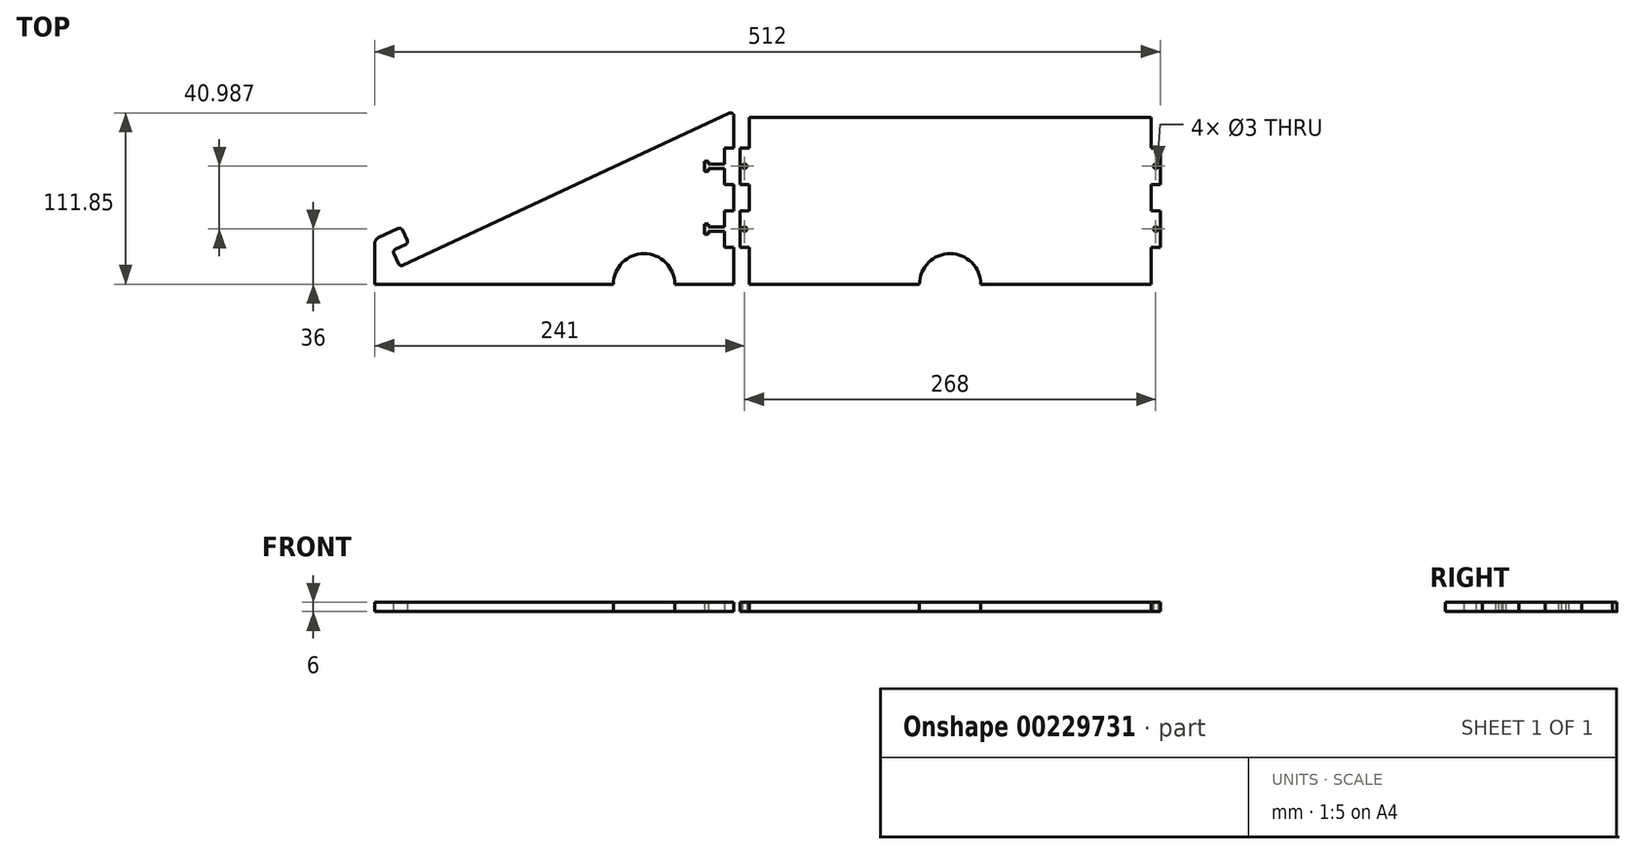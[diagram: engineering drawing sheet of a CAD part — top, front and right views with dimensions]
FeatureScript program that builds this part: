
annotation { "Feature Type Name" : "Feature", "Feature Type Description" : "" }
export const myFeature = defineFeature(function(context is Context, id is Id, definition is map)
    precondition{}
    {
        {
            assignVariable(context, id + "F0", {"name" : "MaterialThickness", "anyValue" : 6});
        }
        {
            var Q0;
            Q0=qCreatedBy(makeId("Top.planeOp"),FACE);
            var sketch = newSketch(context, id + "F1", { "sketchPlane" : qUnion([Q0])});
            skLineSegment(sketch, "E0", {"start": v(20.1, 25.94) * mm, "end": v(13.31, 22.77) * mm});
            skLineSegment(sketch, "E1", {"start": v(12.35, 20.1) * mm, "end": v(15.51, 13.31) * mm});
            skLineSegment(sketch, "E2", {"start": v(18.17, 12.35) * mm, "end": v(231.15, 111.66) * mm});
            skLineSegment(sketch, "E3", {"start": v(234, 0) * mm, "end": v(234, 109.85) * mm});
            skLineSegment(sketch, "E4", {"start": v(244, 108.99) * mm, "end": v(244, 88.99) * mm});
            skLineSegment(sketch, "E5", {"start": v(244, 0) * mm, "end": v(355, 0) * mm});
            skLineSegment(sketch, "E6", {"start": v(506, 0) * mm, "end": v(506, 24) * mm});
            skLineSegment(sketch, "E7", {"start": v(234, 24) * mm, "end": v(228, 24) * mm});
            skLineSegment(sketch, "E8", {"start": v(228, 24) * mm, "end": v(228, 34.5) * mm});
            skLineSegment(sketch, "E9", {"start": v(228, 48) * mm, "end": v(234, 48) * mm});
            skLineSegment(sketch, "E10", {"start": v(234, 56.5) * mm, "end": v(112.85, 56.5) * mm, "construction": true});
            skLineSegment(sketch, "E11.MirrorCS", {"start": v(228, 64.99) * mm, "end": v(234, 64.99) * mm});
            skLineSegment(sketch, "E12.MirrorCS", {"start": v(228, 88.99) * mm, "end": v(228, 78.49) * mm});
            skLineSegment(sketch, "E13.MirrorCS", {"start": v(234, 88.99) * mm, "end": v(228, 88.99) * mm});
            skLineSegment(sketch, "E14", {"start": v(244, 24) * mm, "end": v(238, 24) * mm});
            skLineSegment(sketch, "E15", {"start": v(238, 24) * mm, "end": v(238, 48) * mm});
            skLineSegment(sketch, "E16", {"start": v(238, 48) * mm, "end": v(244, 48) * mm});
            skLineSegment(sketch, "E17.MirrorCS", {"start": v(238, 64.99) * mm, "end": v(244, 64.99) * mm});
            skLineSegment(sketch, "E18.MirrorCS", {"start": v(238, 88.99) * mm, "end": v(238, 64.99) * mm});
            skLineSegment(sketch, "E19.MirrorCS", {"start": v(244, 88.99) * mm, "end": v(238, 88.99) * mm});
            skLineSegment(sketch, "E20", {"start": v(375, 108.99) * mm, "end": v(375, 0) * mm, "construction": true});
            skLineSegment(sketch, "E21.MirrorCS", {"start": v(506, 88.99) * mm, "end": v(512, 88.99) * mm});
            skLineSegment(sketch, "E22.MirrorCS", {"start": v(506, 24) * mm, "end": v(512, 24) * mm});
            skLineSegment(sketch, "E23.MirrorCS", {"start": v(512, 64.99) * mm, "end": v(506, 64.99) * mm});
            skLineSegment(sketch, "E24.MirrorCS", {"start": v(512, 24) * mm, "end": v(512, 48) * mm});
            skLineSegment(sketch, "E25.MirrorCS", {"start": v(512, 48) * mm, "end": v(506, 48) * mm});
            skLineSegment(sketch, "E26.MirrorCS", {"start": v(512, 88.99) * mm, "end": v(512, 64.99) * mm});
            skLineSegment(sketch, "E27", {"start": v(244, 108.99) * mm, "end": v(506, 108.99) * mm});
            skPoint(sketch, "E28.visualSharp", {"position": v(17.06, 37.2) * mm});
            skPoint(sketch, "E29.visualSharp", {"position": v(21.92, 26.78) * mm});
            skPoint(sketch, "E30.visualSharp", {"position": v(234, 112.99) * mm});
            skArc(sketch, "E30.filletArc", {"start": v(234, 109.85) * mm, "mid": v(233.07, 111.53) * mm, "end": v(231.15, 111.66) * mm});
            skCircle(sketch, "E31", {"center": v(241, 76.99) * mm, "radius": 1.5 * mm});
            skPoint(sketch, "E31.centerSnap0", {"position": v(238, 76.99) * mm});
            skPoint(sketch, "E31.centerSnap1", {"position": v(241, 88.99) * mm});
            skCircle(sketch, "E32.MirrorC", {"center": v(241, 36) * mm, "radius": 1.5 * mm});
            skLineSegment(sketch, "E33", {"start": v(228, 76.99) * mm, "end": v(234, 76.99) * mm, "construction": true});
            skLineSegment(sketch, "E34", {"start": v(228, 75.49) * mm, "end": v(217.5, 75.49) * mm});
            skLineSegment(sketch, "E35", {"start": v(217.5, 75.49) * mm, "end": v(217.5, 73.74) * mm});
            skLineSegment(sketch, "E36", {"start": v(217.5, 73.74) * mm, "end": v(215, 73.74) * mm});
            skLineSegment(sketch, "E37", {"start": v(215, 73.74) * mm, "end": v(215, 76.99) * mm});
            skLineSegment(sketch, "E38.MirrorCS", {"start": v(228, 78.49) * mm, "end": v(217.5, 78.49) * mm});
            skLineSegment(sketch, "E39.MirrorCS", {"start": v(217.5, 78.49) * mm, "end": v(217.5, 80.24) * mm});
            skLineSegment(sketch, "E40.MirrorCS", {"start": v(217.5, 80.24) * mm, "end": v(215, 80.24) * mm});
            skLineSegment(sketch, "E41.MirrorCS", {"start": v(215, 80.24) * mm, "end": v(215, 76.99) * mm});
            skLineSegment(sketch, "E42.MirrorCS", {"start": v(215, 39.25) * mm, "end": v(215, 36) * mm});
            skLineSegment(sketch, "E43.MirrorCS", {"start": v(228, 37.5) * mm, "end": v(217.5, 37.5) * mm});
            skLineSegment(sketch, "E44.MirrorCS", {"start": v(215, 32.75) * mm, "end": v(215, 36) * mm});
            skLineSegment(sketch, "E45.MirrorCS", {"start": v(217.5, 37.5) * mm, "end": v(217.5, 39.25) * mm});
            skLineSegment(sketch, "E46.MirrorCS", {"start": v(217.5, 34.5) * mm, "end": v(217.5, 32.75) * mm});
            skLineSegment(sketch, "E47.MirrorCS", {"start": v(217.5, 32.75) * mm, "end": v(215, 32.75) * mm});
            skLineSegment(sketch, "E48.MirrorCS", {"start": v(228, 34.5) * mm, "end": v(217.5, 34.5) * mm});
            skLineSegment(sketch, "E49.MirrorCS", {"start": v(217.5, 39.25) * mm, "end": v(215, 39.25) * mm});
            skCircle(sketch, "E50.MirrorC", {"center": v(509, 36) * mm, "radius": 1.5 * mm});
            skCircle(sketch, "E51.MirrorC", {"center": v(509, 76.99) * mm, "radius": 1.5 * mm});
            skPoint(sketch, "E52.orphan", {"position": v(244, 112.99) * mm});
            skPoint(sketch, "E53.orphan", {"position": v(506, 112.99) * mm});
            skPoint(sketch, "E54.orphan", {"position": v(375, 112.99) * mm});
            skPoint(sketch, "E55.visualSharp", {"position": v(16.36, 11.5) * mm});
            skArc(sketch, "E55.filletArc", {"start": v(15.51, 13.31) * mm, "mid": v(16.64, 12.28) * mm, "end": v(18.17, 12.35) * mm});
            skPoint(sketch, "E56.visualSharp", {"position": v(11.5, 21.92) * mm});
            skArc(sketch, "E56.filletArc", {"start": v(13.31, 22.77) * mm, "mid": v(12.28, 21.64) * mm, "end": v(12.35, 20.1) * mm});
            skArc(sketch, "E57", {"start": v(395, 0) * mm, "mid": v(375, 20) * mm, "end": v(355, 0) * mm});
            skLineSegment(sketch, "E58.trimOffspring", {"start": v(395, 0) * mm, "end": v(506, 0) * mm});
            skLineSegment(sketch, "E59.trimOffspring", {"start": v(228, 75.49) * mm, "end": v(228, 64.99) * mm});
            skLineSegment(sketch, "E60.trimOffspring", {"start": v(228, 37.5) * mm, "end": v(228, 48) * mm});
            skLineSegment(sketch, "E61.trimOffspring", {"start": v(244, 64.99) * mm, "end": v(244, 48) * mm});
            skLineSegment(sketch, "E62.trimOffspring", {"start": v(244, 24) * mm, "end": v(244, 0) * mm});
            skLineSegment(sketch, "E63.trimOffspring", {"start": v(506, 88.99) * mm, "end": v(506, 108.99) * mm});
            skLineSegment(sketch, "E64.trimOffspring", {"start": v(506, 48) * mm, "end": v(506, 64.99) * mm});
            skLineSegment(sketch, "E65", {"start": v(234, 0) * mm, "end": v(195.5, 0) * mm});
            skPoint(sketch, "E66", {"position": v(117, 0) * mm});
            skPoint(sketch, "E67", {"position": v(175.5, 0) * mm});
            skArc(sketch, "E68", {"start": v(195.5, 0) * mm, "mid": v(175.5, 20) * mm, "end": v(155.5, 0) * mm});
            skLineSegment(sketch, "E69.trimOffspring", {"start": v(155.5, 0) * mm, "end": v(0, 0) * mm});
            skLineSegment(sketch, "E70", {"start": v(15.25, 36.36) * mm, "end": v(2.3, 30.33) * mm});
            skLineSegment(sketch, "E71", {"start": v(0, 0) * mm, "end": v(0, 26.7) * mm});
            skLineSegment(sketch, "E72", {"start": v(21.08, 28.6) * mm, "end": v(17.9, 35.4) * mm});
            skArc(sketch, "E73.filletArc", {"start": v(20.1, 25.94) * mm, "mid": v(21.14, 27.07) * mm, "end": v(21.08, 28.6) * mm});
            skArc(sketch, "E74.filletArc", {"start": v(17.9, 35.4) * mm, "mid": v(16.78, 36.43) * mm, "end": v(15.25, 36.36) * mm});
            skPoint(sketch, "E75.visualSharp", {"position": v(0, 29.25) * mm});
            skArc(sketch, "E75.filletArc", {"start": v(2.3, 30.33) * mm, "mid": v(0.63, 28.85) * mm, "end": v(0, 26.7) * mm});
            skSolve(sketch);
        }
        {
            var Q0;
            Q0=makeQuery(id+"F1.imprint","IMPRINT",FACE,{"disambiguationData":[TD([[makeQuery(id+"F1.imprint","IMPRINT",EDGE,{"derivedFrom":sQuery(id+"F1.wireOp",EDGE,"E0")}),-1.0]])]});
            var Q1;
            {var subQ10=sQuery(id+"F1.wireOp",EDGE,"E5");Q1=makeQuery(id+"F1.imprint","IMPRINT",FACE,{"disambiguationData":[TD([[makeQuery(id+"F1.imprint","IMPRINT",EDGE,{"derivedFrom":subQ10}),1.0]])]});}
            var Q2;
            {var subQ0=sQuery(id+"F1.wireOp",EDGE,"E14");Q2=makeQuery(id+"F1.imprint","IMPRINT",FACE,{"disambiguationData":[TD([[makeQuery(id+"F1.imprint","IMPRINT",EDGE,{"derivedFrom":subQ0}),-1.0]])]});}
            var Q3;
            {var subQ0=sQuery(id+"F1.wireOp",EDGE,"E17.MirrorCS");Q3=makeQuery(id+"F1.imprint","IMPRINT",FACE,{"disambiguationData":[TD([[makeQuery(id+"F1.imprint","IMPRINT",EDGE,{"derivedFrom":subQ0}),1.0]])]});}
            var Q4;
            {var subQ0=sQuery(id+"F1.wireOp",EDGE,"E21.MirrorCS");Q4=makeQuery(id+"F1.imprint","IMPRINT",FACE,{"disambiguationData":[TD([[makeQuery(id+"F1.imprint","IMPRINT",EDGE,{"derivedFrom":subQ0}),-1.0]])]});}
            var Q5;
            {var subQ0=sQuery(id+"F1.wireOp",EDGE,"E22.MirrorCS");Q5=makeQuery(id+"F1.imprint","IMPRINT",FACE,{"disambiguationData":[TD([[makeQuery(id+"F1.imprint","IMPRINT",EDGE,{"derivedFrom":subQ0}),1.0]])]});}
            extrude(context, id + "F2", {"entities" : qUnion([Q0, Q1, Q2, Q3, Q4, Q5]), "depth" : (getVariable(context, 'MaterialThickness')) * mm});
        }
    });
